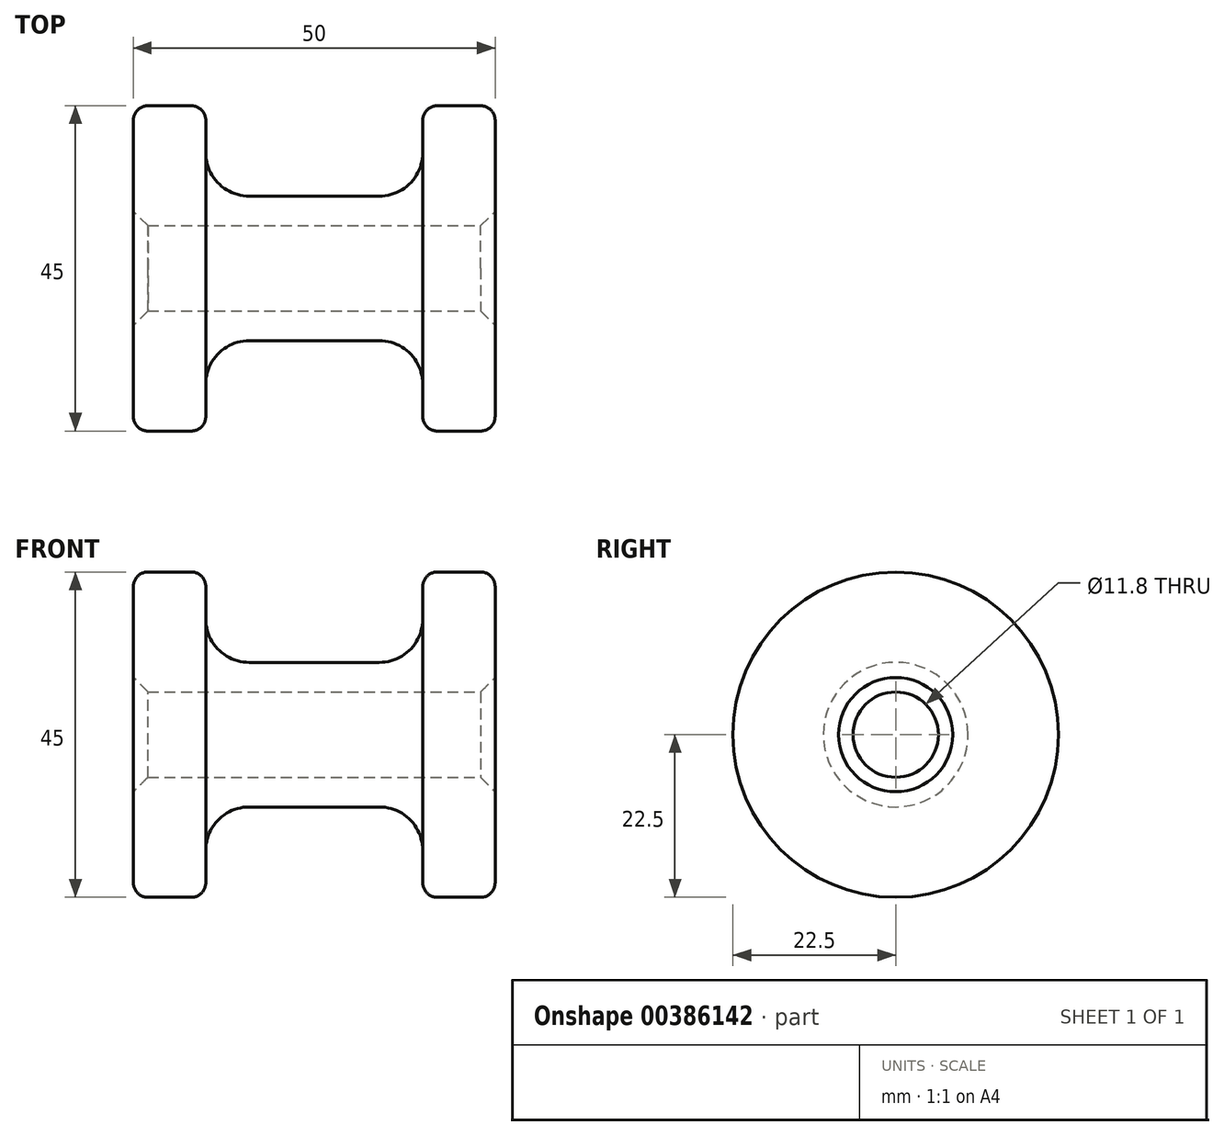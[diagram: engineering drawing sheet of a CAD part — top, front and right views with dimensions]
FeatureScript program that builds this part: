
annotation { "Feature Type Name" : "Feature", "Feature Type Description" : "" }
export const myFeature = defineFeature(function(context is Context, id is Id, definition is map)
    precondition{}
    {
        {
            var Q0;
            Q0=qCreatedBy(makeId("Front.planeOp"),FACE);
            var sketch = newSketch(context, id + "F0", { "sketchPlane" : qUnion([Q0])});
            skLineSegment(sketch, "E0", {"start": v(0, 20.5) * mm, "end": v(0, 0) * mm});
            skLineSegment(sketch, "E1", {"start": v(50, 0) * mm, "end": v(50, 20.5) * mm});
            skLineSegment(sketch, "E2", {"start": v(48, 22.5) * mm, "end": v(42, 22.5) * mm});
            skLineSegment(sketch, "E3", {"start": v(40, 20.5) * mm, "end": v(40, 16) * mm});
            skLineSegment(sketch, "E4", {"start": v(34, 10) * mm, "end": v(16, 10) * mm});
            skLineSegment(sketch, "E5", {"start": v(10, 16) * mm, "end": v(10, 20.5) * mm});
            skLineSegment(sketch, "E6", {"start": v(8, 22.5) * mm, "end": v(2, 22.5) * mm});
            skPoint(sketch, "E7.visualSharp", {"position": v(10, 10) * mm});
            skArc(sketch, "E7.filletArc", {"start": v(10, 16) * mm, "mid": v(11.76, 11.76) * mm, "end": v(16, 10) * mm});
            skPoint(sketch, "E8.visualSharp", {"position": v(40, 10) * mm});
            skArc(sketch, "E8.filletArc", {"start": v(34, 10) * mm, "mid": v(38.24, 11.76) * mm, "end": v(40, 16) * mm});
            skPoint(sketch, "E9.visualSharp", {"position": v(10, 22.5) * mm});
            skArc(sketch, "E9.filletArc", {"start": v(10, 20.5) * mm, "mid": v(9.41, 21.91) * mm, "end": v(8, 22.5) * mm});
            skPoint(sketch, "E10.visualSharp", {"position": v(40, 22.5) * mm});
            skArc(sketch, "E10.filletArc", {"start": v(42, 22.5) * mm, "mid": v(40.59, 21.91) * mm, "end": v(40, 20.5) * mm});
            skPoint(sketch, "E11.visualSharp", {"position": v(50, 22.5) * mm});
            skArc(sketch, "E11.filletArc", {"start": v(50, 20.5) * mm, "mid": v(49.41, 21.91) * mm, "end": v(48, 22.5) * mm});
            skPoint(sketch, "E12.visualSharp", {"position": v(0, 22.5) * mm});
            skArc(sketch, "E12.filletArc", {"start": v(2, 22.5) * mm, "mid": v(0.59, 21.91) * mm, "end": v(0, 20.5) * mm});
            skLineSegment(sketch, "E13", {"start": v(0, 0) * mm, "end": v(50, 0) * mm});
            skSolve(sketch);
        }
        {
            var Q0;
            Q0=makeQuery(id+"F0.imprint","IMPRINT",FACE,{"disambiguationData":[TD([[makeQuery(id+"F0.imprint","IMPRINT",EDGE,{"derivedFrom":sQuery(id+"F0.wireOp",EDGE,"E0")}),1.0]])]});
            var Q1;
            Q1=sQuery(id+"F0.wireOp",EDGE,"E13");
            revolve(context, id + "F1", {"entities" : qUnion([Q0]), "axis" : qUnion([Q1]), "revolveType" : RevolveType.FULL});
        }
        {
            var Q0;
            Q0=makeQuery(id+"F1.opRevolve","SWEPT_FACE",FACE,{"disambiguationData":[OSD([sQuery(id+"F0.wireOp",EDGE,"E1")])]});
            var sketch = newSketch(context, id + "F2", { "sketchPlane" : qUnion([Q0])});
            skCircle(sketch, "E14", {"center": v(0, 0) * mm, "radius": 5.9 * mm});
            skSolve(sketch);
        }
        {
            var Q0;
            Q0=makeQuery(id+"F2.imprint","IMPRINT",FACE,{"disambiguationData":[TD([[makeQuery(id+"F2.imprint","IMPRINT",EDGE,{"derivedFrom":sQuery(id+"F2.wireOp",EDGE,"E14")}),1.0]])]});
            extrude(context, id + "F3", {"entities" : qUnion([Q0]), "operationType" : NewBodyOperationType.REMOVE, "endBound" : BoundingType.THROUGH_ALL, "oppositeDirection" : true, "depth" : 25 * mm});
        }
        {
            var Q0;
            Q0=makeQuery(id+"F3.boolean.opBoolean","COPY",FACE,{"derivedFrom":makeQuery(id+"F3.opExtrude","SWEPT_FACE",FACE,{"disambiguationData":[OSD([sQuery(id+"F2.wireOp",EDGE,"E14")])]})});
            chamfer(context, id + "F4", {"entities" : qUnion([Q0]), "width" : 2 * mm, "tangentPropagation" : true});
        }
    });
